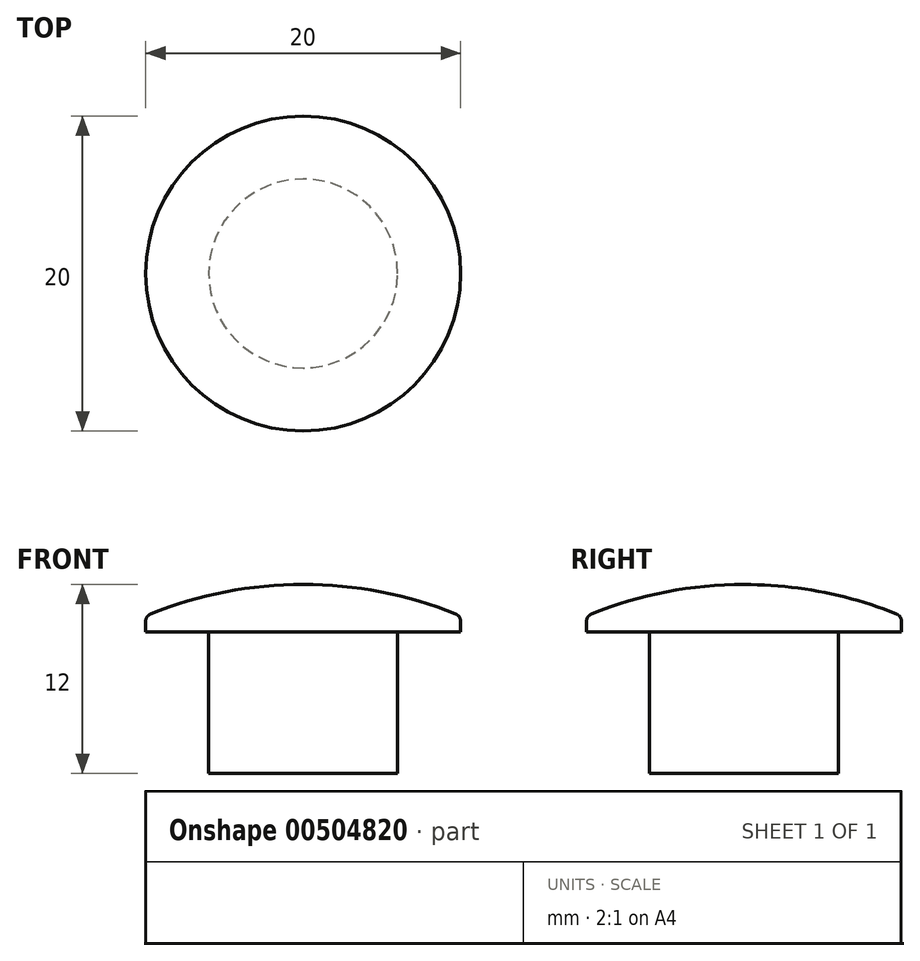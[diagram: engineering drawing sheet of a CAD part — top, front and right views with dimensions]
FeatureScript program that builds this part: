
annotation { "Feature Type Name" : "Feature", "Feature Type Description" : "" }
export const myFeature = defineFeature(function(context is Context, id is Id, definition is map)
    precondition{}
    {
        {
            var Q0;
            Q0=qCreatedBy(makeId("Right.planeOp"),FACE);
            var sketch = newSketch(context, id + "F0", { "sketchPlane" : qUnion([Q0])});
            skLineSegment(sketch, "E0", {"start": v(0, 0) * mm, "end": v(-6, 0) * mm});
            skLineSegment(sketch, "E1", {"start": v(-6, 0) * mm, "end": v(-6, 9) * mm});
            skLineSegment(sketch, "E2", {"start": v(-6, 9) * mm, "end": v(-10, 9) * mm});
            skLineSegment(sketch, "E3", {"start": v(-10, 9) * mm, "end": v(-10, 10) * mm, "construction": true});
            skLineSegment(sketch, "E4", {"start": v(-10, 10) * mm, "end": v(0, 10) * mm, "construction": true});
            skArc(sketch, "E5", {"start": v(0, 12) * mm, "mid": v(-5.1, 11.5) * mm, "end": v(-10, 10) * mm, "construction": true});
            skLineSegment(sketch, "E6", {"start": v(0, 12) * mm, "end": v(0, 0) * mm});
            skLineSegment(sketch, "E7", {"start": v(0, 12) * mm, "end": v(4.07, 12) * mm, "construction": true});
            skArc(sketch, "E8", {"start": v(-9.69, 10.13) * mm, "mid": v(-9.91, 9.94) * mm, "end": v(-10, 9.66) * mm});
            skLineSegment(sketch, "E9", {"start": v(-10, 9.66) * mm, "end": v(-10, 9) * mm});
            skArc(sketch, "E10", {"start": v(-9.69, 10.13) * mm, "mid": v(-4.93, 11.53) * mm, "end": v(0, 12) * mm});
            skSolve(sketch);
        }
        {
            var Q0;
            Q0 = qSketchRegion(id + "F0", true);
            var Q1;
            Q1=sQuery(id+"F0.wireOp",EDGE,"E6");
            revolve(context, id + "F1", {"entities" : qUnion([Q0]), "axis" : qUnion([Q1]), "revolveType" : RevolveType.FULL});
        }
    });
